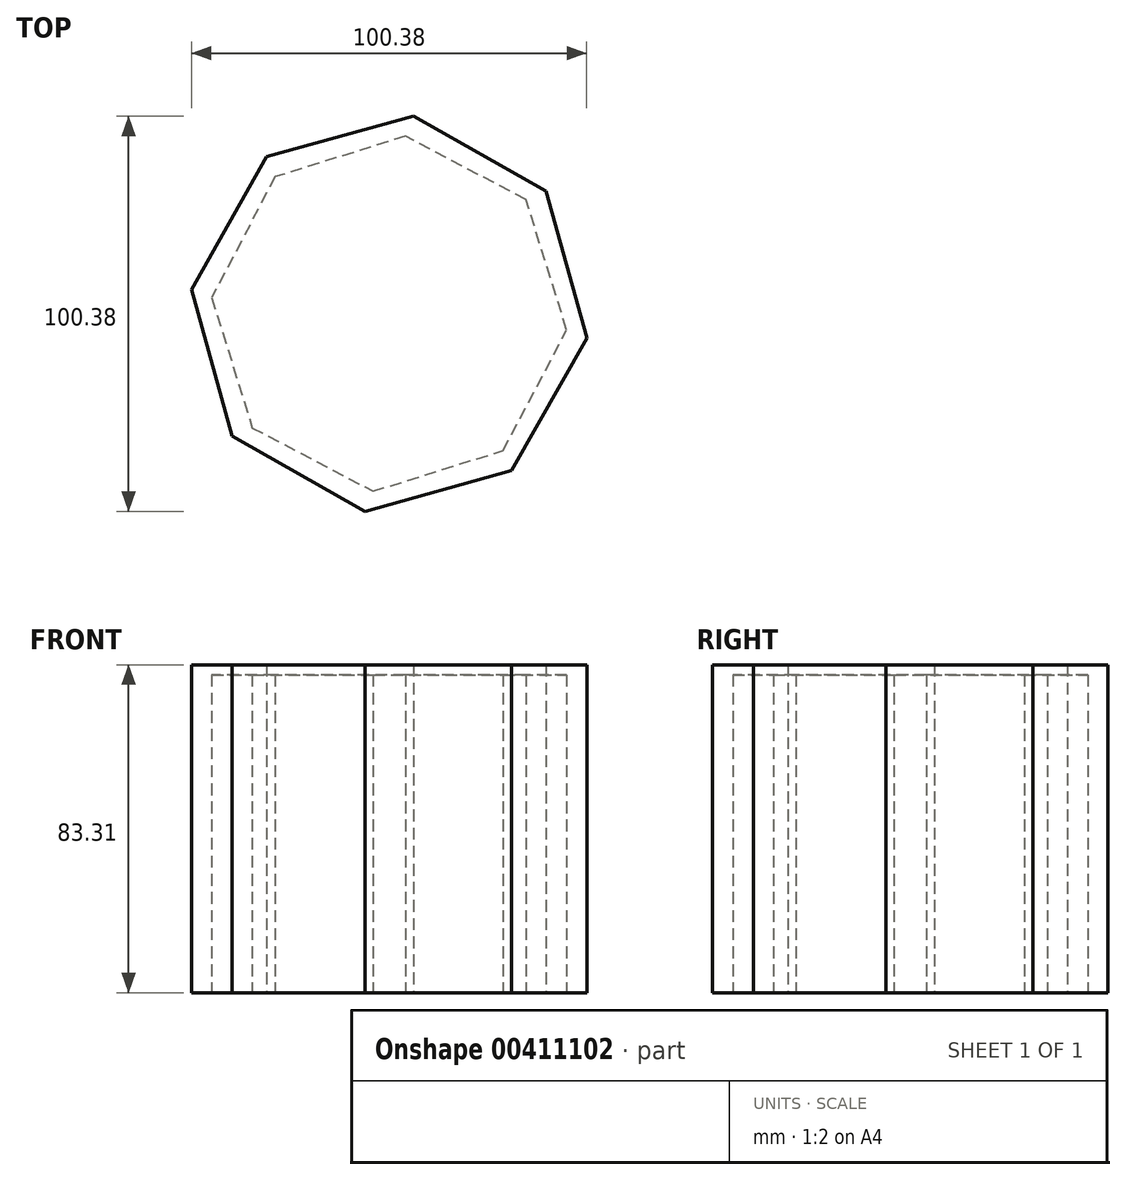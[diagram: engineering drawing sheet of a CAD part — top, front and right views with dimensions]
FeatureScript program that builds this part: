
annotation { "Feature Type Name" : "Feature", "Feature Type Description" : "" }
export const myFeature = defineFeature(function(context is Context, id is Id, definition is map)
    precondition{}
    {
        {
            var Q0;
            Q0=qCreatedBy(makeId("Top.planeOp"),FACE);
            var sketch = newSketch(context, id + "F0", { "sketchPlane" : qUnion([Q0])});
            skCircle(sketch, "E0.cCircle", {"center": v(0, 0) * mm, "radius": 46.72 * mm, "construction": true});
            skLineSegment(sketch, "E0.0", {"start": v(-50.2, 6.18) * mm, "end": v(-31.12, 39.86) * mm});
            skLineSegment(sketch, "E0.1", {"start": v(-31.12, 39.86) * mm, "end": v(6.18, 50.2) * mm});
            skLineSegment(sketch, "E0.2", {"start": v(6.18, 50.2) * mm, "end": v(39.86, 31.12) * mm});
            skLineSegment(sketch, "E0.3", {"start": v(39.86, 31.12) * mm, "end": v(50.2, -6.18) * mm});
            skLineSegment(sketch, "E0.4", {"start": v(50.2, -6.18) * mm, "end": v(31.12, -39.86) * mm});
            skLineSegment(sketch, "E0.5", {"start": v(31.12, -39.86) * mm, "end": v(-6.18, -50.2) * mm});
            skLineSegment(sketch, "E0.6", {"start": v(-6.18, -50.2) * mm, "end": v(-39.86, -31.12) * mm});
            skLineSegment(sketch, "E0.7", {"start": v(-39.86, -31.12) * mm, "end": v(-50.2, 6.18) * mm});
            skPoint(sketch, "E0.0.midPoint", {"position": v(-40.66, 23.02) * mm});
            skSolve(sketch);
        }
        {
            var Q0;
            Q0 = qSketchRegion(id + "F0", true);
            extrude(context, id + "F1", {"entities" : qUnion([Q0]), "depth" : 83.31 * mm});
        }
        {
            var Q0;
            Q0=makeQuery(id+"F1.opExtrude","CAP_FACE",FACE,{"disambiguationData":[OSD([sQuery(id+"F0.wireOp",EDGE,"E0.0"),sQuery(id+"F0.wireOp",EDGE,"E0.1"),sQuery(id+"F0.wireOp",EDGE,"E0.2"),sQuery(id+"F0.wireOp",EDGE,"E0.3"),sQuery(id+"F0.wireOp",EDGE,"E0.4"),sQuery(id+"F0.wireOp",EDGE,"E0.5"),sQuery(id+"F0.wireOp",EDGE,"E0.6"),sQuery(id+"F0.wireOp",EDGE,"E0.7")])],"isStart":true});
            var sketch = newSketch(context, id + "F2", { "sketchPlane" : qUnion([Q0])});
            skCircle(sketch, "E1.cCircle", {"center": v(0, 0) * mm, "radius": 41.83 * mm, "construction": true});
            skLineSegment(sketch, "E1.0", {"start": v(-34.79, 28.98) * mm, "end": v(-4.1, 45.09) * mm});
            skLineSegment(sketch, "E1.1", {"start": v(-4.1, 45.09) * mm, "end": v(28.98, 34.79) * mm});
            skLineSegment(sketch, "E1.2", {"start": v(28.98, 34.79) * mm, "end": v(45.09, 4.1) * mm});
            skLineSegment(sketch, "E1.3", {"start": v(45.09, 4.1) * mm, "end": v(34.79, -28.98) * mm});
            skLineSegment(sketch, "E1.4", {"start": v(34.79, -28.98) * mm, "end": v(4.1, -45.09) * mm});
            skLineSegment(sketch, "E1.5", {"start": v(4.1, -45.09) * mm, "end": v(-28.98, -34.79) * mm});
            skLineSegment(sketch, "E1.6", {"start": v(-28.98, -34.79) * mm, "end": v(-45.09, -4.1) * mm});
            skLineSegment(sketch, "E1.7", {"start": v(-45.09, -4.1) * mm, "end": v(-34.79, 28.98) * mm});
            skPoint(sketch, "E1.0.midPoint", {"position": v(-19.45, 37.03) * mm});
            skSolve(sketch);
        }
        {
            var Q0;
            Q0=makeQuery(id+"F2.imprint","IMPRINT",FACE,{"disambiguationData":[TD([[makeQuery(id+"F2.imprint","IMPRINT",EDGE,{"derivedFrom":sQuery(id+"F2.wireOp",EDGE,"E1.0")}),-1.0]])]});
            extrude(context, id + "F3", {"entities" : qUnion([Q0]), "operationType" : NewBodyOperationType.REMOVE, "oppositeDirection" : true, "depth" : 80.77 * mm});
        }
    });
